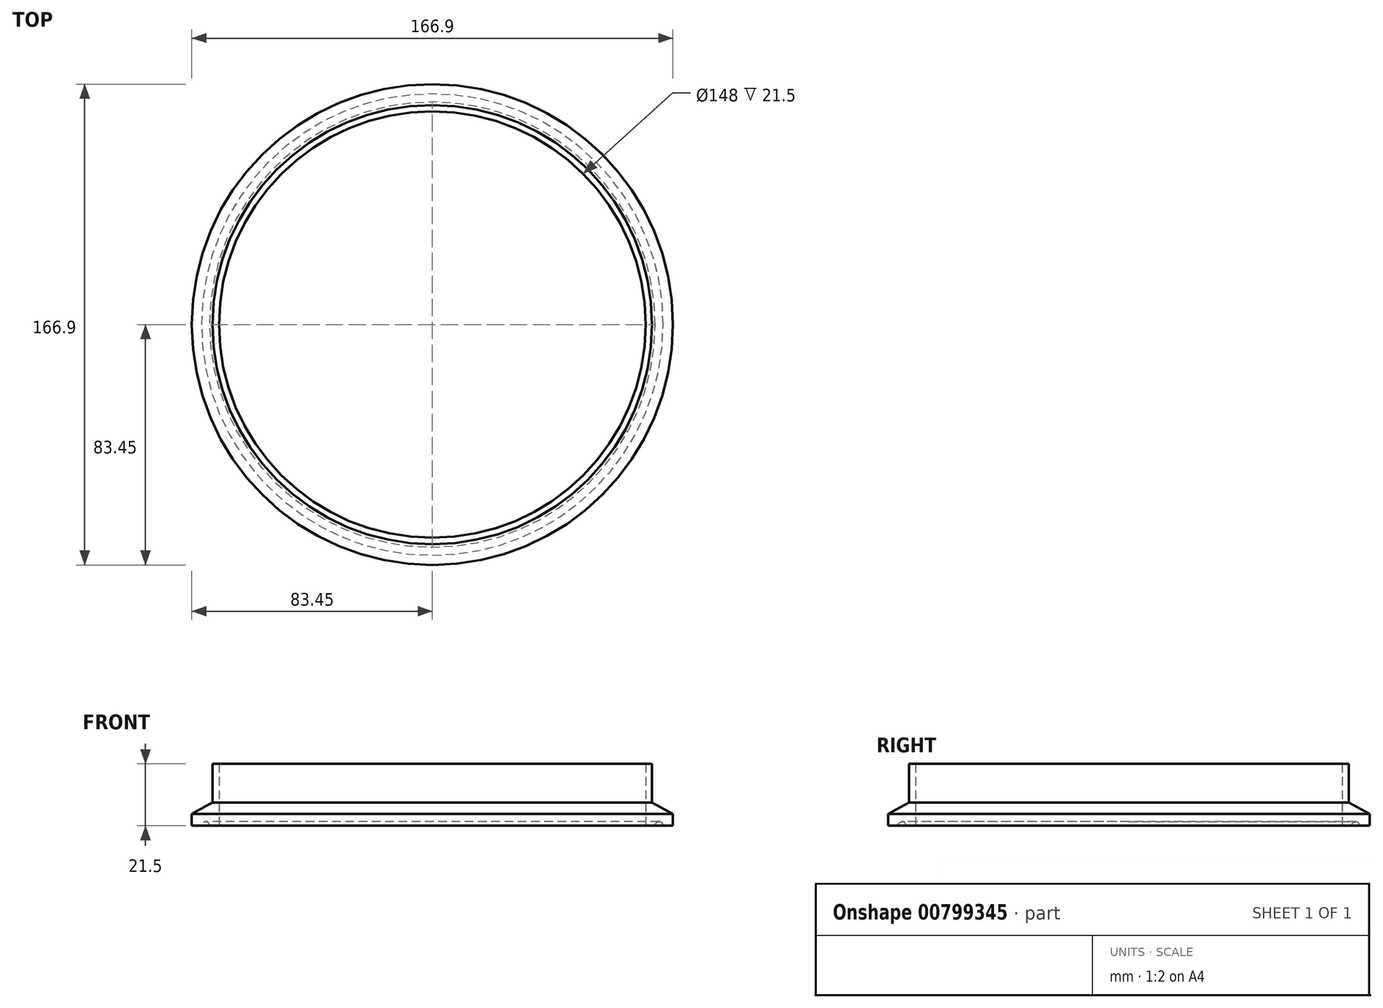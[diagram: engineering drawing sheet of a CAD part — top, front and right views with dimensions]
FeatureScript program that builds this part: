
annotation { "Feature Type Name" : "Feature", "Feature Type Description" : "" }
export const myFeature = defineFeature(function(context is Context, id is Id, definition is map)
    precondition{}
    {
        {
            var Q0;
            Q0=qCreatedBy(makeId("Front.planeOp"),FACE);
            var sketch = newSketch(context, id + "F0", { "sketchPlane" : qUnion([Q0])});
            skLineSegment(sketch, "E0", {"start": v(-80.05, -0.8) * mm, "end": v(-83.13, -0.8) * mm});
            skLineSegment(sketch, "E1", {"start": v(-76.2, 20.7) * mm, "end": v(-74, 20.7) * mm});
            skLineSegment(sketch, "E2", {"start": v(-74, 20.7) * mm, "end": v(-74, -0.8) * mm});
            skLineSegment(sketch, "E3", {"start": v(-77.25, -0.8) * mm, "end": v(-74, -0.8) * mm});
            skLineSegment(sketch, "E4", {"start": v(-83.45, -0.8) * mm, "end": v(-83.45, 3.33) * mm});
            skLineSegment(sketch, "E5", {"start": v(-76.2, 7.3) * mm, "end": v(-83.45, 3.33) * mm});
            skLineSegment(sketch, "E6.trimOffspring", {"start": v(-83.13, -0.8) * mm, "end": v(-83.45, -0.8) * mm});
            skLineSegment(sketch, "E7", {"start": v(0, 0) * mm, "end": v(0, 38.79) * mm, "construction": true});
            skArc(sketch, "E8", {"start": v(-77.25, -0.8) * mm, "mid": v(-78.65, 0.6) * mm, "end": v(-80.05, -0.8) * mm});
            skLineSegment(sketch, "E9", {"start": v(-76.2, 20.7) * mm, "end": v(-76.2, 7.3) * mm});
            skSolve(sketch);
        }
        {
            var Q0;
            Q0=qSketchRegion(id+"F0",true);
            var Q1;
            Q1=sQuery(id+"F0.wireOp",EDGE,"E7");
            revolve(context, id + "F1", {"entities" : qUnion([Q0]), "axis" : qUnion([Q1]), "revolveType" : RevolveType.FULL});
        }
    });
